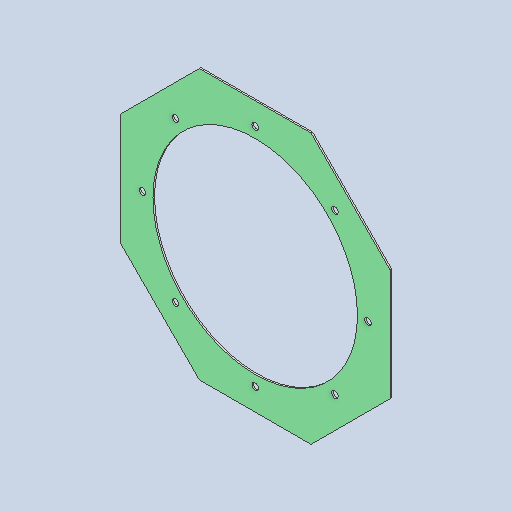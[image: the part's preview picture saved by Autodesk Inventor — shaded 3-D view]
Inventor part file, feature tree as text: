
AUTODESK INVENTOR PART (.ipt)
format: ipt  version: 2025 (Build 290162010, 162A)  size: 172,032 bytes
history: native  units: mm
features: sketch x2, other x2, sheet_metal_op x1, extrude x1, pattern_circular x1
ambient origin geometry x8: Origin, YZ Plane, XZ Plane, XY Plane, X Axis, Y Axis, Z Axis, Center Point
bodies: Solid1 (feature_tree)
feature tree (7):
  sheet_metal_op  "Face1"
  extrude  "Extrusion1"  Depth=3.0mm
  pattern_circular  "Circular Pattern1"  [2 undecoded]
  sketch  "Sketch2"  dims[d15=3.0mm d16=12.5mm]
  other  "Plate1"
  sketch  "Sketch4"  dims[d17=214.5mm d18=10.0mm d19=0.0mm d20=80.0mm d21=360.0deg d23=513.0mm d26=389.0mm]
  other  "Definition1"
note: 2 required parameter values undecoded (feature->parameter linkage not recoverable at this tier; creation-order binding heuristic only, values carry confidence <= 0.55)
